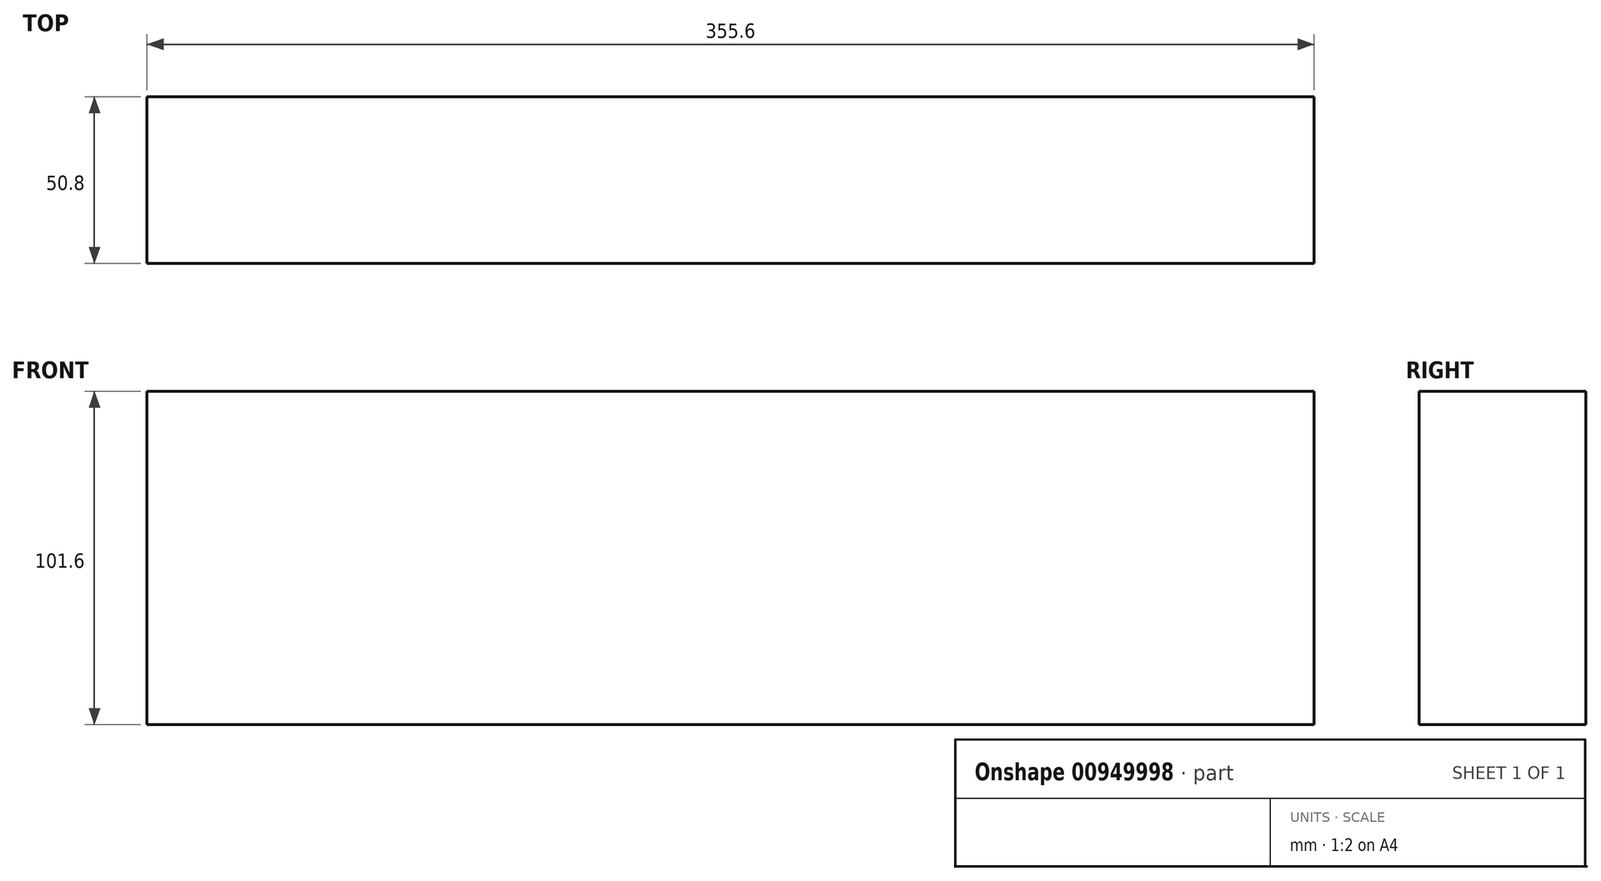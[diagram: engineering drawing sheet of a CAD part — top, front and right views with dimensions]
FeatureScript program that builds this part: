
annotation { "Feature Type Name" : "Feature", "Feature Type Description" : "" }
export const myFeature = defineFeature(function(context is Context, id is Id, definition is map)
    precondition{}
    {
        {
            var Q0;
            Q0=qCreatedBy(makeId("Right.planeOp"),FACE);
            var sketch = newSketch(context, id + "F0", { "sketchPlane" : qUnion([Q0])});
            skLineSegment(sketch, "E0.bottom", {"start": v(0, 101.6) * mm, "end": v(-50.8, 101.6) * mm});
            skLineSegment(sketch, "E0.top", {"start": v(0, 0) * mm, "end": v(-50.8, 0) * mm});
            skLineSegment(sketch, "E0.left", {"start": v(0, 101.6) * mm, "end": v(0, 0) * mm});
            skLineSegment(sketch, "E0.right", {"start": v(-50.8, 101.6) * mm, "end": v(-50.8, 0) * mm});
            skSolve(sketch);
        }
        {
            var Q0;
            Q0=qSketchRegion(id+"F0",true);
            extrude(context, id + "F1", {"entities" : qUnion([Q0]), "endBound" : BoundingType.SYMMETRIC, "depth" : 355.6 * mm, "offsetDistance" : 25.4 * mm});
        }
    });
